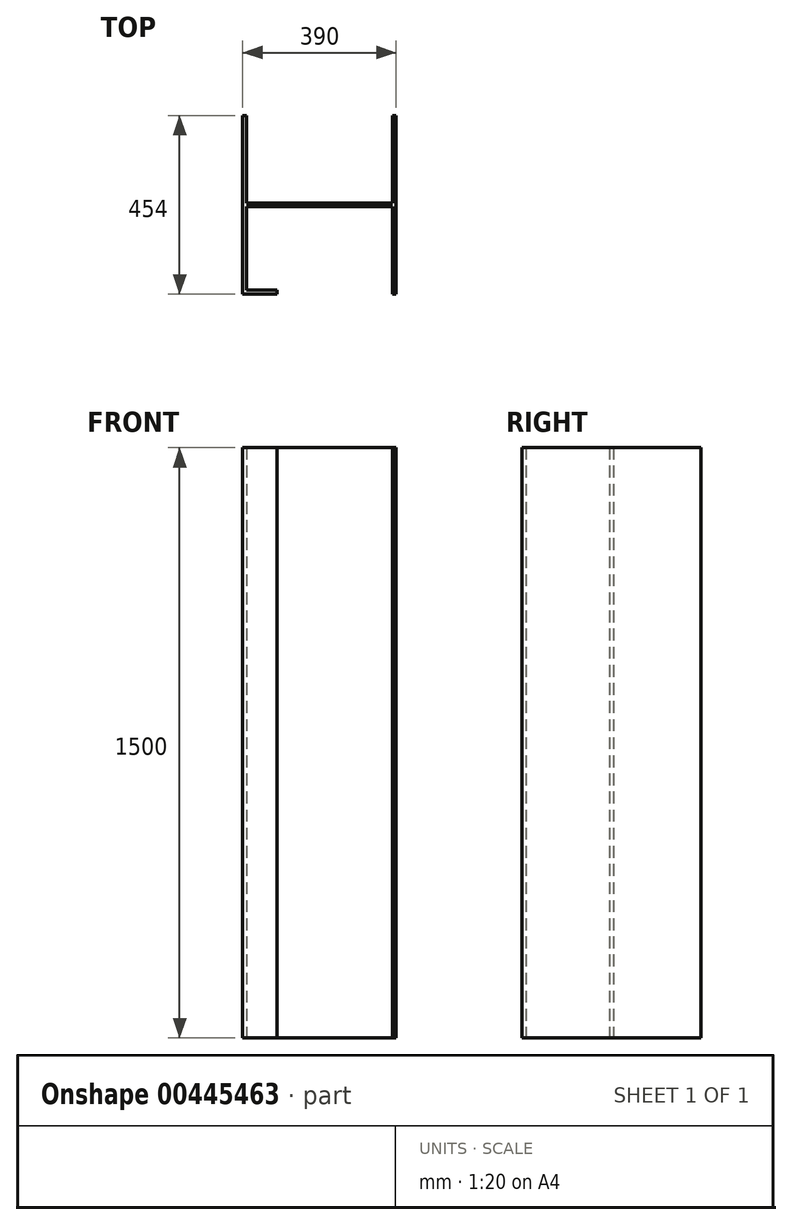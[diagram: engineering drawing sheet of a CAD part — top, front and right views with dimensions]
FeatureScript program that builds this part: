
annotation { "Feature Type Name" : "Feature", "Feature Type Description" : "" }
export const myFeature = defineFeature(function(context is Context, id is Id, definition is map)
    precondition{}
    {
        {
            var Q0;
            Q0=qCreatedBy(makeId("Top.planeOp"),FACE);
            var sketch = newSketch(context, id + "F0", { "sketchPlane" : qUnion([Q0])});
            skLineSegment(sketch, "E0.bottom", {"start": v(195, -227) * mm, "end": v(185, -227) * mm});
            skLineSegment(sketch, "E0.left", {"start": v(195, -227) * mm, "end": v(195, 227) * mm});
            skLineSegment(sketch, "E0.right", {"start": v(-195, -227) * mm, "end": v(-195, 227) * mm});
            skPoint(sketch, "E0.middle", {"position": v(0, 0) * mm});
            skLineSegment(sketch, "E1.top", {"start": v(-108.17, -217) * mm, "end": v(-185, -217) * mm});
            skLineSegment(sketch, "E1.left", {"start": v(185, 217) * mm, "end": v(185, -217) * mm});
            skLineSegment(sketch, "E1.right", {"start": v(-185, 217) * mm, "end": v(-185, -217) * mm});
            skLineSegment(sketch, "E2", {"start": v(-108.17, -227) * mm, "end": v(-108.17, -217) * mm});
            skLineSegment(sketch, "E3", {"start": v(185, -217) * mm, "end": v(185, -227) * mm});
            skLineSegment(sketch, "E4.trimOffspring", {"start": v(-108.17, -227) * mm, "end": v(-195, -227) * mm});
            skLineSegment(sketch, "E5.bottom", {"start": v(185, -5) * mm, "end": v(-185, -5) * mm});
            skLineSegment(sketch, "E5.top", {"start": v(185, 5) * mm, "end": v(-185, 5) * mm});
            skLineSegment(sketch, "E5.left", {"start": v(185, -5) * mm, "end": v(185, 5) * mm});
            skLineSegment(sketch, "E5.right", {"start": v(-185, -5) * mm, "end": v(-185, 5) * mm});
            skLineSegment(sketch, "E6", {"start": v(-185, 217) * mm, "end": v(-185, 227) * mm});
            skLineSegment(sketch, "E7", {"start": v(185, 217) * mm, "end": v(185, 227) * mm});
            skLineSegment(sketch, "E8", {"start": v(-195, 227) * mm, "end": v(-185, 227) * mm});
            skLineSegment(sketch, "E9", {"start": v(185, 227) * mm, "end": v(195, 227) * mm});
            skSolve(sketch);
        }
        {
            var Q0;
            Q0 = qSketchRegion(id + "F0", true);
            extrude(context, id + "F1", {"entities" : qUnion([Q0]), "depth" : 1500 * mm, "offsetDistance" : 25 * mm});
        }
    });
